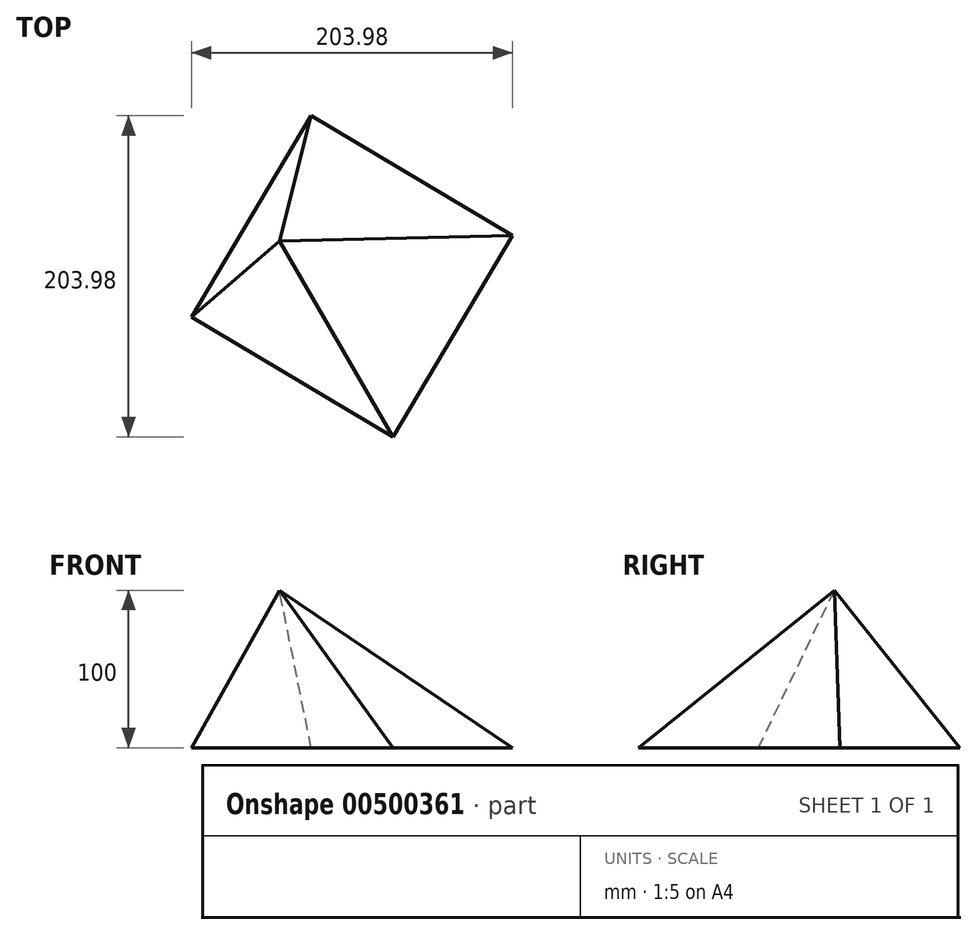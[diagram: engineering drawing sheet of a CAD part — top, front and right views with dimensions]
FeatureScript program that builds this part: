
annotation { "Feature Type Name" : "Feature", "Feature Type Description" : "" }
export const myFeature = defineFeature(function(context is Context, id is Id, definition is map)
    precondition{}
    {
        {
            var Q0;
            Q0=qCreatedBy(makeId("Top.planeOp"),FACE);
            var sketch = newSketch(context, id + "F0", { "sketchPlane" : qUnion([Q0])});
            skCircle(sketch, "E0.cCircle", {"center": v(0, 0) * mm, "radius": 74.42 * mm, "construction": true});
            skLineSegment(sketch, "E0.0", {"start": v(101.99, 25.96) * mm, "end": v(25.96, -101.99) * mm});
            skLineSegment(sketch, "E0.1", {"start": v(25.96, -101.99) * mm, "end": v(-101.99, -25.96) * mm});
            skLineSegment(sketch, "E0.2", {"start": v(-101.99, -25.96) * mm, "end": v(-25.96, 101.99) * mm});
            skLineSegment(sketch, "E0.3", {"start": v(-25.96, 101.99) * mm, "end": v(101.99, 25.96) * mm});
            skPoint(sketch, "E0.0.midPoint", {"position": v(63.98, -38.01) * mm});
            skSolve(sketch);
        }
        {
            var Q0;
            Q0=qCreatedBy(makeId("Top.planeOp"),FACE);
            cPlane(context, id + "F1", {"entities" : qUnion([Q0]), "cplaneType" : CPlaneType.OFFSET, "offset" : 100 * mm, "width" : 150 * mm, "height" : 150 * mm});
        }
        {
            var Q0;
            Q0=qCreatedBy(id+"F1.planeOp",FACE);
            var sketch = newSketch(context, id + "F2", { "sketchPlane" : qUnion([Q0])});
            skPoint(sketch, "E1", {"position": v(-46.14, 22.3) * mm});
            skSolve(sketch);
        }
        {
            var Q0;
            Q0=makeQuery(id+"F0.imprint","IMPRINT",FACE,{"disambiguationData":[TD([[makeQuery(id+"F0.imprint","IMPRINT",EDGE,{"derivedFrom":sQuery(id+"F0.wireOp",EDGE,"E0.0")}),-1.0]])]});
            var Q1;
            Q1=sQuery(id+"F2.wireOp",VERTEX,"E1");
            loft(context, id + "F3", {"sheetProfilesArray" : [{ "sheetProfileEntities" : qUnion([Q0]) }, { "sheetProfileEntities" : qUnion([Q1]) }]});
        }
    });
